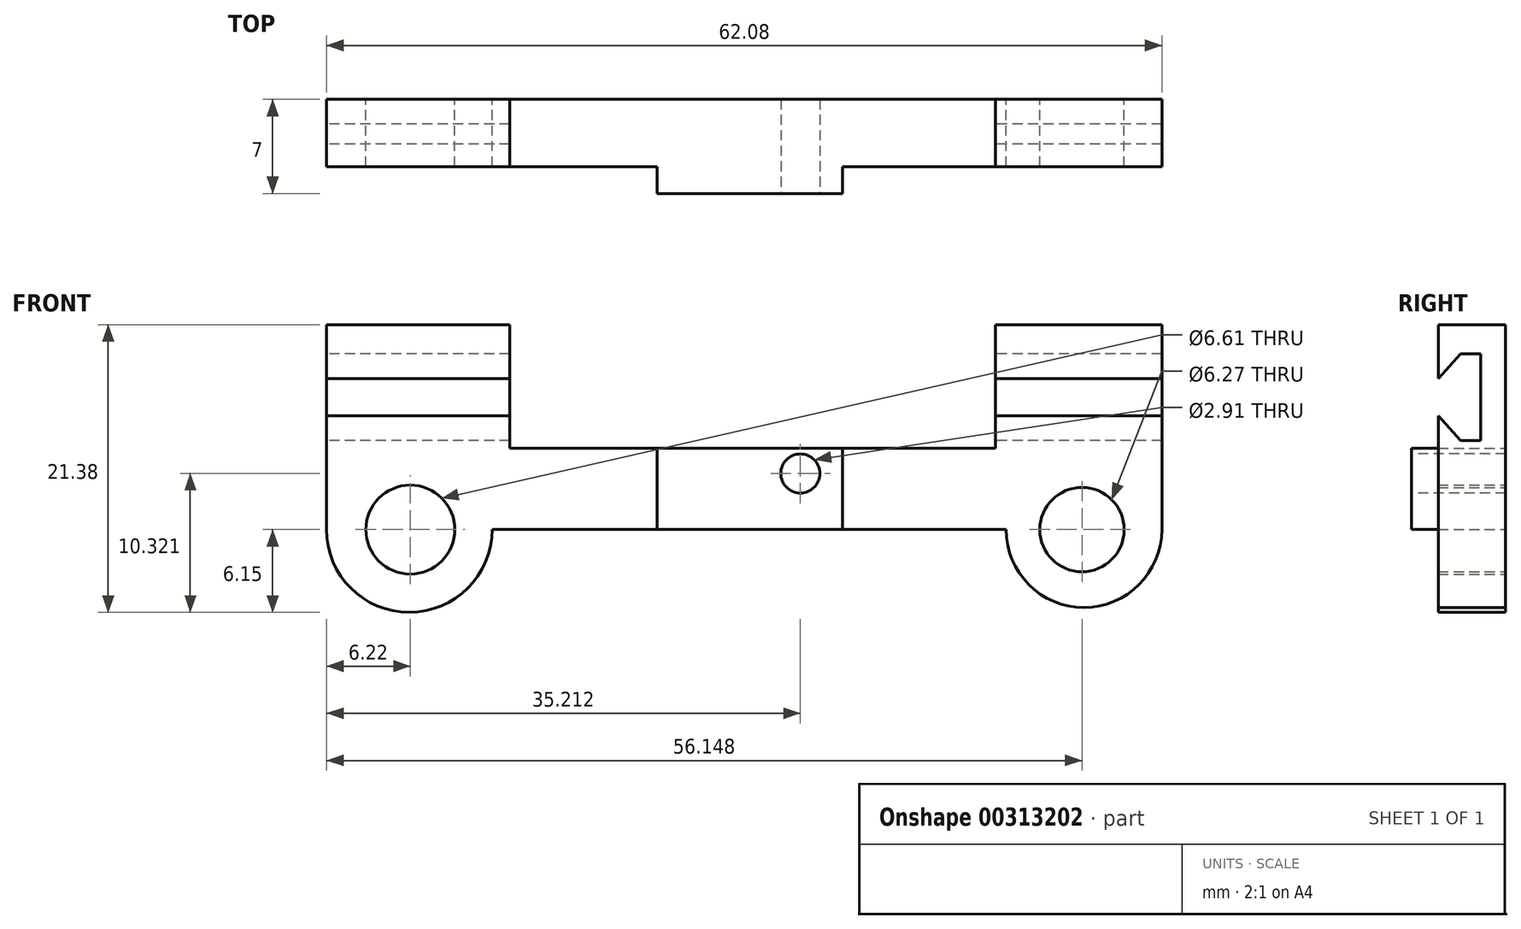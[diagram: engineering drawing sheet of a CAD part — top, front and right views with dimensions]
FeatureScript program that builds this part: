
annotation { "Feature Type Name" : "Feature", "Feature Type Description" : "" }
export const myFeature = defineFeature(function(context is Context, id is Id, definition is map)
    precondition{}
    {
        {
            var Q0;
            Q0=qCreatedBy(makeId("Front.planeOp"),FACE);
            var sketch = newSketch(context, id + "F0", { "sketchPlane" : qUnion([Q0])});
            skCircle(sketch, "E0", {"center": v(-25.22, 0) * mm, "radius": 3.3 * mm});
            skCircle(sketch, "E1", {"center": v(24.7, 0) * mm, "radius": 3.14 * mm});
            skArc(sketch, "E2", {"start": v(-31.44, 0) * mm, "mid": v(-25.3, -6.15) * mm, "end": v(-19.14, 0) * mm});
            skArc(sketch, "E3", {"start": v(19.06, 0) * mm, "mid": v(24.85, -5.79) * mm, "end": v(30.64, 0) * mm});
            skLineSegment(sketch, "E4", {"start": v(-31.44, 0) * mm, "end": v(-31.44, 15.23) * mm});
            skLineSegment(sketch, "E5", {"start": v(-31.44, 15.23) * mm, "end": v(-17.83, 15.23) * mm});
            skLineSegment(sketch, "E6", {"start": v(-17.83, 15.23) * mm, "end": v(-17.83, 6.05) * mm});
            skLineSegment(sketch, "E7", {"start": v(-17.83, 6.05) * mm, "end": v(18.27, 6.05) * mm});
            skLineSegment(sketch, "E8", {"start": v(18.27, 6.05) * mm, "end": v(18.27, 15.23) * mm});
            skLineSegment(sketch, "E9", {"start": v(18.27, 15.23) * mm, "end": v(30.64, 15.23) * mm});
            skLineSegment(sketch, "E10", {"start": v(30.64, 15.23) * mm, "end": v(30.64, 0) * mm});
            skLineSegment(sketch, "E11", {"start": v(19.06, 0) * mm, "end": v(-19.14, 0) * mm});
            skSolve(sketch);
        }
        {
            var Q0;
            Q0=qSketchRegion(id+"F0",true);
            extrude(context, id + "F1", {"entities" : qUnion([Q0]), "depth" : 5 * mm});
        }
        {
            var Q0;
            Q0=makeQuery(id+"F1.opExtrude","SWEPT_FACE",FACE,{"disambiguationData":[OSD([sQuery(id+"F0.wireOp",EDGE,"E4")])]});
            var sketch = newSketch(context, id + "F2", { "sketchPlane" : qUnion([Q0])});
            skLineSegment(sketch, "E12", {"start": v(1.84, 13.06) * mm, "end": v(1.84, 6.63) * mm});
            skLineSegment(sketch, "E13", {"start": v(1.84, 13.06) * mm, "end": v(3.34, 13.06) * mm});
            skLineSegment(sketch, "E14", {"start": v(3.34, 13.06) * mm, "end": v(5, 11.23) * mm});
            skLineSegment(sketch, "E15", {"start": v(1.84, 6.63) * mm, "end": v(3.34, 6.63) * mm});
            skLineSegment(sketch, "E16", {"start": v(3.34, 6.63) * mm, "end": v(5, 8.46) * mm});
            skSolve(sketch);
        }
        {
            var Q0;
            Q0=makeQuery(id+"F2.imprint","IMPRINT",FACE,{"disambiguationData":[TD([[makeQuery(id+"F2.imprint","IMPRINT",EDGE,{"derivedFrom":sQuery(id+"F2.wireOp",EDGE,"E12")}),1.0]])]});
            extrude(context, id + "F3", {"entities" : qUnion([Q0]), "operationType" : NewBodyOperationType.REMOVE, "endBound" : BoundingType.THROUGH_ALL, "oppositeDirection" : true, "depth" : 25 * mm});
        }
        {
            var Q0;
            {var subQ0=sQuery(id+"F0.wireOp",EDGE,"E11");var subQ1=sQuery(id+"F0.wireOp",EDGE,"E10");var subQ2=sQuery(id+"F0.wireOp",EDGE,"E8");var subQ3=sQuery(id+"F0.wireOp",EDGE,"E7");var subQ4=sQuery(id+"F0.wireOp",EDGE,"E6");var subQ5=sQuery(id+"F0.wireOp",EDGE,"E4");var subQ6=sQuery(id+"F0.wireOp",EDGE,"E0");var subQ7=sQuery(id+"F0.wireOp",EDGE,"E3");var subQ8=sQuery(id+"F0.wireOp",EDGE,"E1");var subQ9=sQuery(id+"F0.wireOp",EDGE,"E2");Q0=makeQuery(id+"F3.boolean.opBoolean","SPLIT",FACE,{"disambiguationData":[TD([makeQuery(id+"F1.opExtrude","SWEPT_FACE",FACE,{"disambiguationData":[OSD([subQ6])]})])],"derivedFrom":makeQuery(id+"F1.opExtrude","CAP_FACE",FACE,{"disambiguationData":[OSD([subQ6,subQ8,subQ9,subQ7,subQ5,sQuery(id+"F0.wireOp",EDGE,"E5"),subQ4,subQ3,subQ2,sQuery(id+"F0.wireOp",EDGE,"E9"),subQ1,subQ0])],"isStart":false})});}
            var sketch = newSketch(context, id + "F4", { "sketchPlane" : qUnion([Q0])});
            skLineSegment(sketch, "E17.bottom", {"start": v(-6.87, 6.05) * mm, "end": v(6.9, 6.05) * mm});
            skLineSegment(sketch, "E17.top", {"start": v(-6.87, 0) * mm, "end": v(6.9, 0) * mm});
            skLineSegment(sketch, "E17.left", {"start": v(-6.87, 6.05) * mm, "end": v(-6.87, 0) * mm});
            skLineSegment(sketch, "E17.right", {"start": v(6.9, 6.05) * mm, "end": v(6.9, 0) * mm});
            skSolve(sketch);
        }
        {
            var Q0;
            Q0=qSketchRegion(id+"F4",true);
            extrude(context, id + "F5", {"entities" : qUnion([Q0]), "operationType" : NewBodyOperationType.ADD, "depth" : 2 * mm});
        }
        {
            var Q0;
            Q0=makeQuery(id+"F5.opExtrude","CAP_FACE",FACE,{"disambiguationData":[OSD([sQuery(id+"F4.wireOp",EDGE,"E17.bottom"),sQuery(id+"F4.wireOp",EDGE,"E17.top"),sQuery(id+"F4.wireOp",EDGE,"E17.left"),sQuery(id+"F4.wireOp",EDGE,"E17.right")])],"isStart":false});
            var sketch = newSketch(context, id + "F6", { "sketchPlane" : qUnion([Q0])});
            skCircle(sketch, "E18", {"center": v(3.77, 4.17) * mm, "radius": 1.45 * mm});
            skPoint(sketch, "E18.centerSnap0", {"position": v(6.9, 3.03) * mm});
            skPoint(sketch, "E18.centerSnap1", {"position": v(0.02, 6.05) * mm});
            skSolve(sketch);
        }
        {
            var Q0;
            Q0=qSketchRegion(id+"F6",true);
            extrude(context, id + "F7", {"entities" : qUnion([Q0]), "operationType" : NewBodyOperationType.REMOVE, "oppositeDirection" : true, "depth" : 25 * mm});
        }
    });
